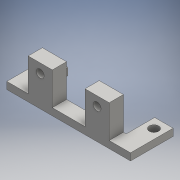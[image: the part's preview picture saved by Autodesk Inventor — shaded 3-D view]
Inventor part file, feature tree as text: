
AUTODESK INVENTOR PART (.ipt)
format: ipt  version: 2016 (Build 200138000, 138)  size: 189,440 bytes
history: native  units: mm
features: sketch x7, extrude x5, hole x2, plane x1
ambient origin geometry x8: Origin, YZ Plane, XZ Plane, XY Plane, X Axis, Y Axis, Z Axis, Center Point
bodies: Solid1 (feature_tree)
feature tree (15):
  sketch  "Sketch1"  dims[d7=2.5mm d13=7.5mm]
  sketch  "Sketch2"  dims[d14=11.5mm d16=2.0mm]
  plane  "Work Plane2"
  sketch  "Sketch3"  dims[d17=3.0mm d23=5.0mm]
  sketch  "Sketch4"  dims[d24=6.5mm d25=29.8mm]
  extrude  "Extrusion1"  Depth=7.5mm
  extrude  "Extrusion2"  Depth=11.5mm
  hole  "Hole1"  [1 undecoded]
  extrude  "Extrusion8"  Depth=6.5mm
  extrude  "Extrusion9"  Depth=18.5mm
  sketch  "Sketch10"  dims[d31=10.1mm d32=6.5mm d33=2.5mm d34=0.0mm d35=2.5mm d36=0.0mm d37=2.8mm d38=6.0mm d39=4.0mm d40=2.0mm d41=90.0deg d42=8.0mm d43=20.594885mm d69=1.75mm d70=0.9mm d71=1.75mm d72=0.9mm d73=2.5mm d74=0.0mm d75=5.0mm d76=0.0mm d95=16.0mm d97=15.0mm d98=6.5mm d99=5.0mm d100=2.5mm d101=0.0mm d102=3.3mm d103=6.0mm d104=4.0mm d105=2.0mm d106=90.0deg d107=8.0mm d108=20.594885mm]
  extrude  "Extrusion10"  [1 undecoded]
  hole  "Hole2"  [1 undecoded]
  sketch  "Sketch5"  dims[d26=13.0mm d27=18.5mm]
  sketch  "Sketch8"  dims[d28=3.2mm d30=-6.75mm]
note: 3 required parameter values undecoded (feature->parameter linkage not recoverable at this tier; creation-order binding heuristic only, values carry confidence <= 0.55)
